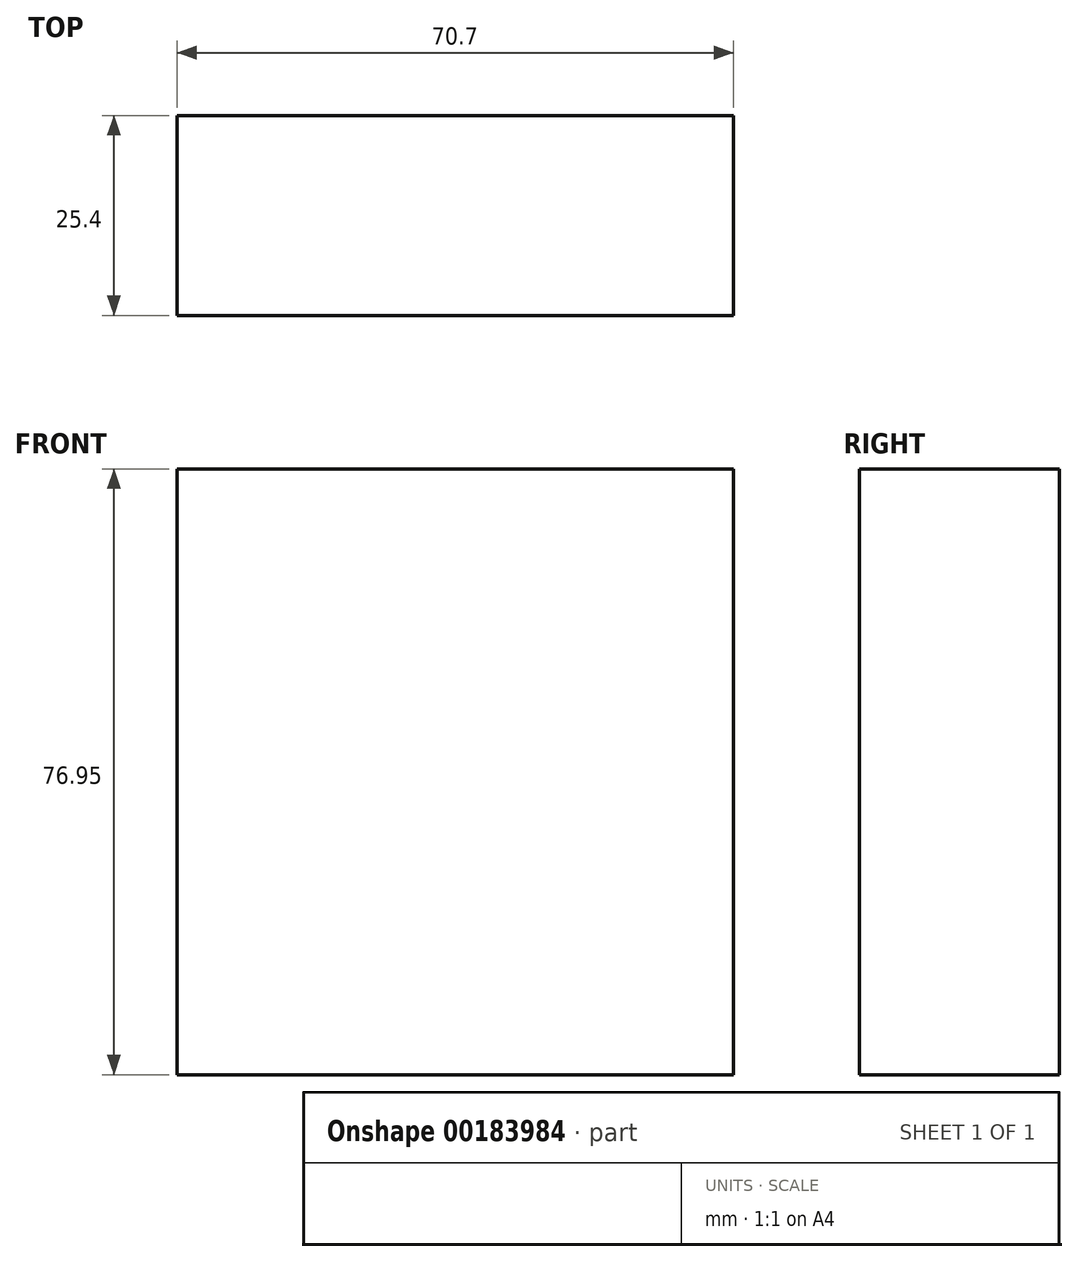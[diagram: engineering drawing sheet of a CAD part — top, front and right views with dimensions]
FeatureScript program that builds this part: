
annotation { "Feature Type Name" : "Feature", "Feature Type Description" : "" }
export const myFeature = defineFeature(function(context is Context, id is Id, definition is map)
    precondition{}
    {
        {
            var Q0;
            Q0=qCreatedBy(makeId("Front.planeOp"),FACE);
            var sketch = newSketch(context, id + "F0", { "sketchPlane" : qUnion([Q0])});
            skLineSegment(sketch, "E0.bottom", {"start": v(-33.22, 40.46) * mm, "end": v(37.48, 40.46) * mm});
            skLineSegment(sketch, "E0.top", {"start": v(-33.22, -36.49) * mm, "end": v(37.48, -36.49) * mm});
            skLineSegment(sketch, "E0.left", {"start": v(-33.22, 40.46) * mm, "end": v(-33.22, -36.49) * mm});
            skLineSegment(sketch, "E0.right", {"start": v(37.48, 40.46) * mm, "end": v(37.48, -36.49) * mm});
            skSolve(sketch);
        }
        {
            var Q0;
            Q0 = qSketchRegion(id + "F0", true);
            extrude(context, id + "F1", {"entities" : qUnion([Q0]), "depth" : 25.4 * mm});
        }
    });
